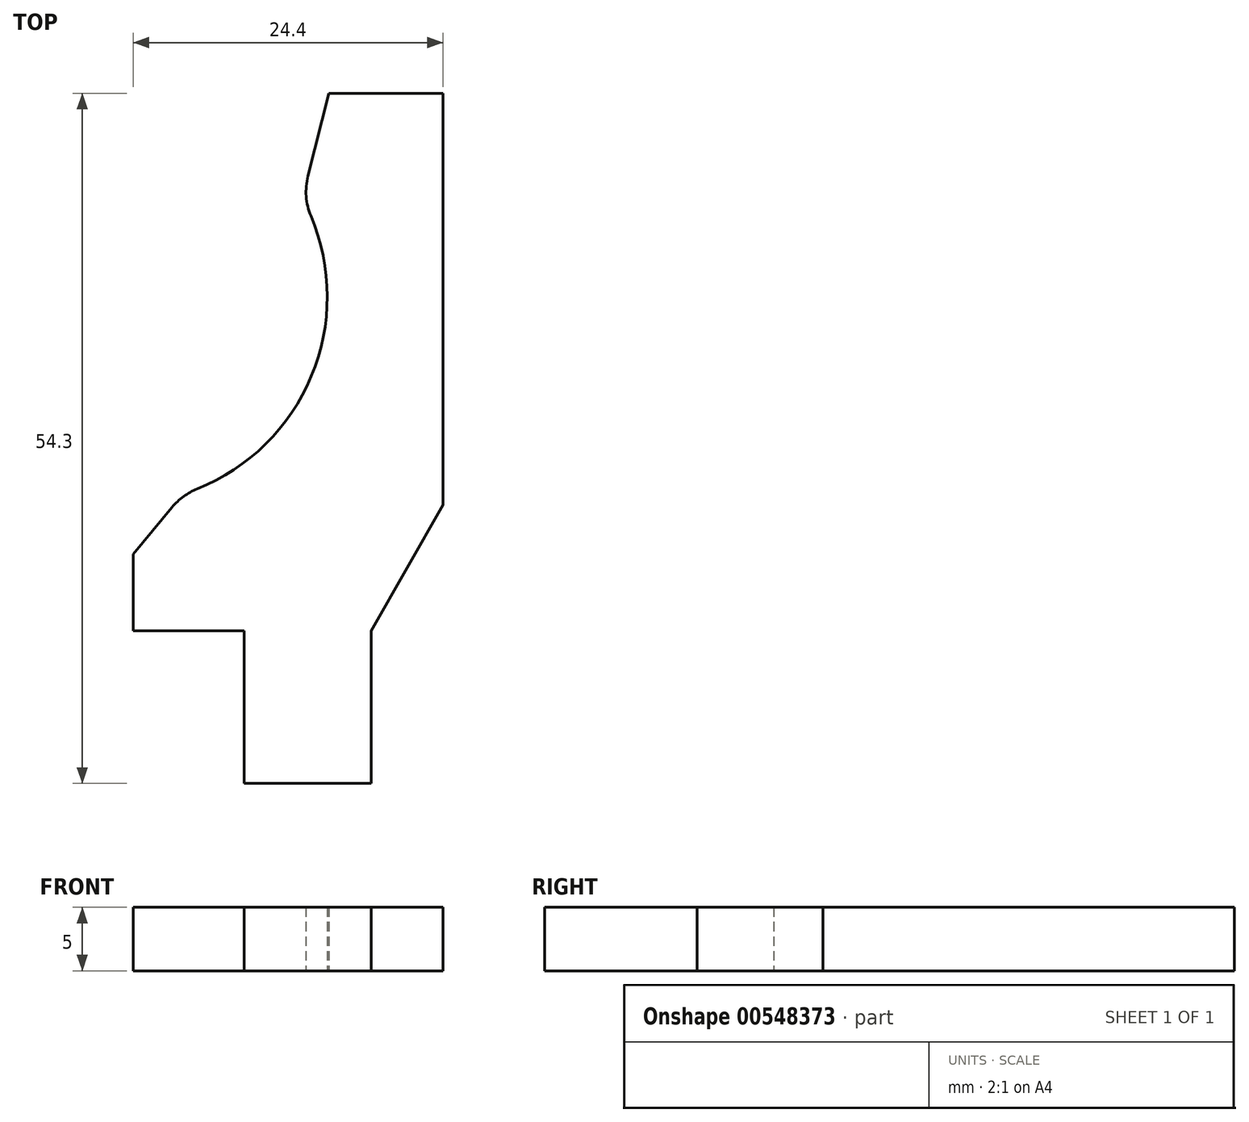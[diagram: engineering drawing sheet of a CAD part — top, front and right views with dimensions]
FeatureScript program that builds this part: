
annotation { "Feature Type Name" : "Feature", "Feature Type Description" : "" }
export const myFeature = defineFeature(function(context is Context, id is Id, definition is map)
    precondition{}
    {
        {
            var Q0;
            Q0=qCreatedBy(makeId("Top.planeOp"),FACE);
            var sketch = newSketch(context, id + "F0", { "sketchPlane" : qUnion([Q0])});
            skArc(sketch, "E0", {"start": v(-7.15, -3.98) * mm, "mid": v(-8.23, -4.58) * mm, "end": v(-9.13, -5.42) * mm});
            skLineSegment(sketch, "E1", {"start": v(-12.2, -9.12) * mm, "end": v(-9.13, -5.42) * mm});
            skLineSegment(sketch, "E2", {"start": v(-12.2, -15.15) * mm, "end": v(-12.2, -9.12) * mm});
            skLineSegment(sketch, "E3", {"start": v(-3.45, -15.15) * mm, "end": v(-12.2, -15.15) * mm});
            skLineSegment(sketch, "E4", {"start": v(-3.45, -27.15) * mm, "end": v(-3.45, -15.15) * mm});
            skLineSegment(sketch, "E5", {"start": v(6.55, -27.15) * mm, "end": v(-3.45, -27.15) * mm});
            skLineSegment(sketch, "E6", {"start": v(6.55, -15.15) * mm, "end": v(6.55, -27.15) * mm});
            skLineSegment(sketch, "E7", {"start": v(12.2, -5.24) * mm, "end": v(6.55, -15.15) * mm});
            skLineSegment(sketch, "E8", {"start": v(12.2, 27.15) * mm, "end": v(12.2, -5.24) * mm});
            skLineSegment(sketch, "E9", {"start": v(3.2, 27.15) * mm, "end": v(12.2, 27.15) * mm});
            skLineSegment(sketch, "E10", {"start": v(1.56, 20.64) * mm, "end": v(3.2, 27.15) * mm});
            skArc(sketch, "E11", {"start": v(1.56, 20.64) * mm, "mid": v(1.43, 19.04) * mm, "end": v(1.8, 17.48) * mm});
            skArc(sketch, "E12", {"start": v(-7.15, -3.98) * mm, "mid": v(1.83, 4.87) * mm, "end": v(1.8, 17.48) * mm});
            skSolve(sketch);
        }
        {
            var Q0;
            Q0=makeQuery(id+"F0.imprint","IMPRINT",FACE,{"disambiguationData":[TD([[makeQuery(id+"F0.imprint","IMPRINT",EDGE,{"derivedFrom":sQuery(id+"F0.wireOp",EDGE,"E0")}),1.0]])]});
            extrude(context, id + "F1", {"entities" : qUnion([Q0]), "depth" : 5 * mm, "offsetDistance" : 25 * mm});
        }
    });
